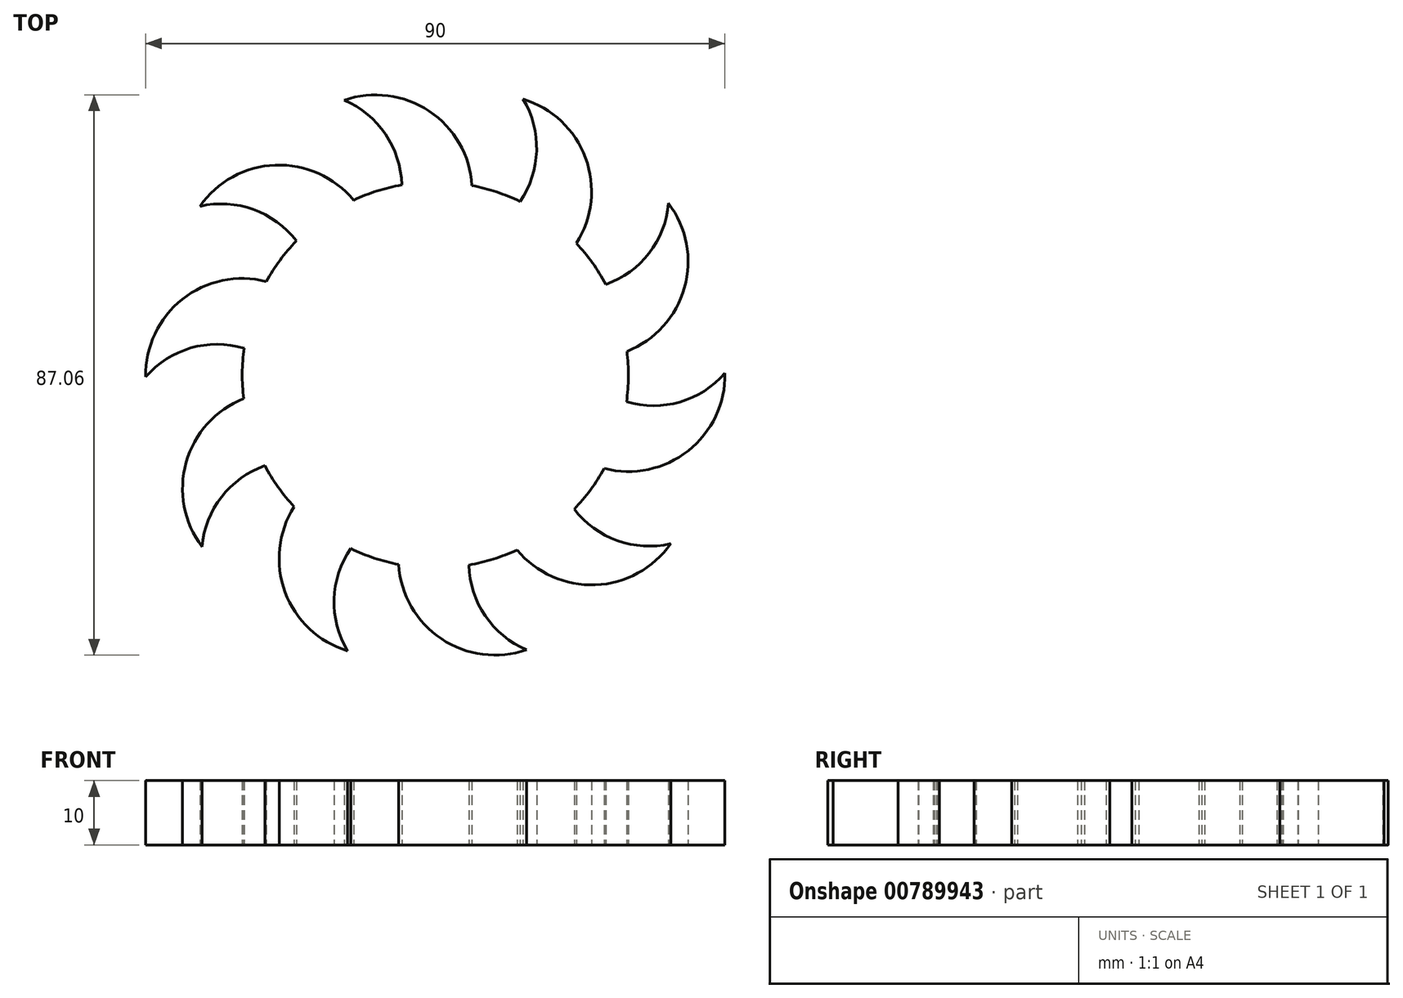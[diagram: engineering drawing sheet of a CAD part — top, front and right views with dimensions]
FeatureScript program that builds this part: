
annotation { "Feature Type Name" : "Feature", "Feature Type Description" : "" }
export const myFeature = defineFeature(function(context is Context, id is Id, definition is map)
    precondition{}
    {
        {
            var Q0;
            Q0=qCreatedBy(makeId("Top.planeOp"),FACE);
            var sketch = newSketch(context, id + "F0", { "sketchPlane" : qUnion([Q0])});
            skArc(sketch, "E0", {"start": v(-29.7, 4.17) * mm, "mid": v(-30, 0.25) * mm, "end": v(-29.77, -3.68) * mm});
            skArc(sketch, "E1", {"start": v(-26.25, 14.52) * mm, "mid": v(-39.3, 11.77) * mm, "end": v(-45, -0.28) * mm});
            skArc(sketch, "E2", {"start": v(-29.7, 4.17) * mm, "mid": v(-38, 4.2) * mm, "end": v(-45, -0.28) * mm});
            skArc(sketch, "E3.1.0", {"start": v(-29.77, -3.68) * mm, "mid": v(-38.71, -13.57) * mm, "end": v(-36.24, -26.68) * mm});
            skArc(sketch, "E3.1.1", {"start": v(-26.49, -14.09) * mm, "mid": v(-33.21, -18.95) * mm, "end": v(-36.24, -26.68) * mm});
            skArc(sketch, "E3.2.0", {"start": v(-21.92, -20.48) * mm, "mid": v(-23.34, -33.74) * mm, "end": v(-13.64, -42.88) * mm});
            skArc(sketch, "E3.2.1", {"start": v(-13.15, -26.97) * mm, "mid": v(-15.73, -34.85) * mm, "end": v(-13.64, -42.88) * mm});
            skArc(sketch, "E3.3.0", {"start": v(-5.7, -29.45) * mm, "mid": v(0.95, -41.01) * mm, "end": v(14.17, -42.7) * mm});
            skArc(sketch, "E3.3.1", {"start": v(5.21, -29.54) * mm, "mid": v(7.76, -37.44) * mm, "end": v(14.17, -42.7) * mm});
            skArc(sketch, "E3.4.0", {"start": v(12.7, -27.18) * mm, "mid": v(24.87, -32.62) * mm, "end": v(36.57, -26.22) * mm});
            skArc(sketch, "E3.4.1", {"start": v(21.58, -20.84) * mm, "mid": v(28.28, -25.73) * mm, "end": v(36.57, -26.22) * mm});
            skArc(sketch, "E3.5.0", {"start": v(26.25, -14.52) * mm, "mid": v(39.3, -11.77) * mm, "end": v(45, 0.28) * mm});
            skArc(sketch, "E3.5.1", {"start": v(29.7, -4.17) * mm, "mid": v(38, -4.2) * mm, "end": v(45, 0.28) * mm});
            skArc(sketch, "E3.6.0", {"start": v(29.77, 3.68) * mm, "mid": v(38.71, 13.57) * mm, "end": v(36.24, 26.68) * mm});
            skArc(sketch, "E3.6.1", {"start": v(26.49, 14.09) * mm, "mid": v(33.21, 18.95) * mm, "end": v(36.24, 26.68) * mm});
            skArc(sketch, "E3.7.0", {"start": v(21.92, 20.48) * mm, "mid": v(23.34, 33.74) * mm, "end": v(13.64, 42.88) * mm});
            skArc(sketch, "E3.7.1", {"start": v(13.15, 26.97) * mm, "mid": v(15.73, 34.85) * mm, "end": v(13.64, 42.88) * mm});
            skArc(sketch, "E3.8.0", {"start": v(5.7, 29.45) * mm, "mid": v(-0.95, 41.01) * mm, "end": v(-14.17, 42.7) * mm});
            skArc(sketch, "E3.8.1", {"start": v(-5.21, 29.54) * mm, "mid": v(-7.76, 37.44) * mm, "end": v(-14.17, 42.7) * mm});
            skArc(sketch, "E3.9.0", {"start": v(-12.7, 27.18) * mm, "mid": v(-24.87, 32.62) * mm, "end": v(-36.57, 26.22) * mm});
            skArc(sketch, "E3.9.1", {"start": v(-21.58, 20.84) * mm, "mid": v(-28.28, 25.73) * mm, "end": v(-36.57, 26.22) * mm});
            skArc(sketch, "E4.trimOffspring", {"start": v(-21.58, 20.84) * mm, "mid": v(-24.12, 17.83) * mm, "end": v(-26.25, 14.52) * mm});
            skArc(sketch, "E5.trimOffspring", {"start": v(-5.21, 29.54) * mm, "mid": v(-9.03, 28.6) * mm, "end": v(-12.7, 27.18) * mm});
            skArc(sketch, "E6.trimOffspring", {"start": v(13.15, 26.97) * mm, "mid": v(9.5, 28.45) * mm, "end": v(5.7, 29.45) * mm});
            skArc(sketch, "E7.trimOffspring", {"start": v(26.49, 14.09) * mm, "mid": v(24.42, 17.43) * mm, "end": v(21.92, 20.48) * mm});
            skArc(sketch, "E8.trimOffspring", {"start": v(29.7, -4.17) * mm, "mid": v(30, -0.25) * mm, "end": v(29.77, 3.68) * mm});
            skArc(sketch, "E9.trimOffspring", {"start": v(21.58, -20.84) * mm, "mid": v(24.12, -17.83) * mm, "end": v(26.25, -14.52) * mm});
            skArc(sketch, "E10.trimOffspring", {"start": v(5.21, -29.54) * mm, "mid": v(9.03, -28.6) * mm, "end": v(12.7, -27.18) * mm});
            skArc(sketch, "E11.trimOffspring", {"start": v(-13.15, -26.97) * mm, "mid": v(-9.5, -28.45) * mm, "end": v(-5.7, -29.45) * mm});
            skArc(sketch, "E12.trimOffspring", {"start": v(-26.49, -14.09) * mm, "mid": v(-24.42, -17.43) * mm, "end": v(-21.92, -20.48) * mm});
            skSolve(sketch);
        }
        {
            var Q0;
            Q0=makeQuery(id+"F0.imprint","IMPRINT",FACE,{"disambiguationData":[TD([[makeQuery(id+"F0.imprint","IMPRINT",EDGE,{"derivedFrom":sQuery(id+"F0.wireOp",EDGE,"E0")}),1.0]])]});
            extrude(context, id + "F1", {"entities" : qUnion([Q0]), "depth" : 10 * mm, "offsetDistance" : 25 * mm});
        }
    });
